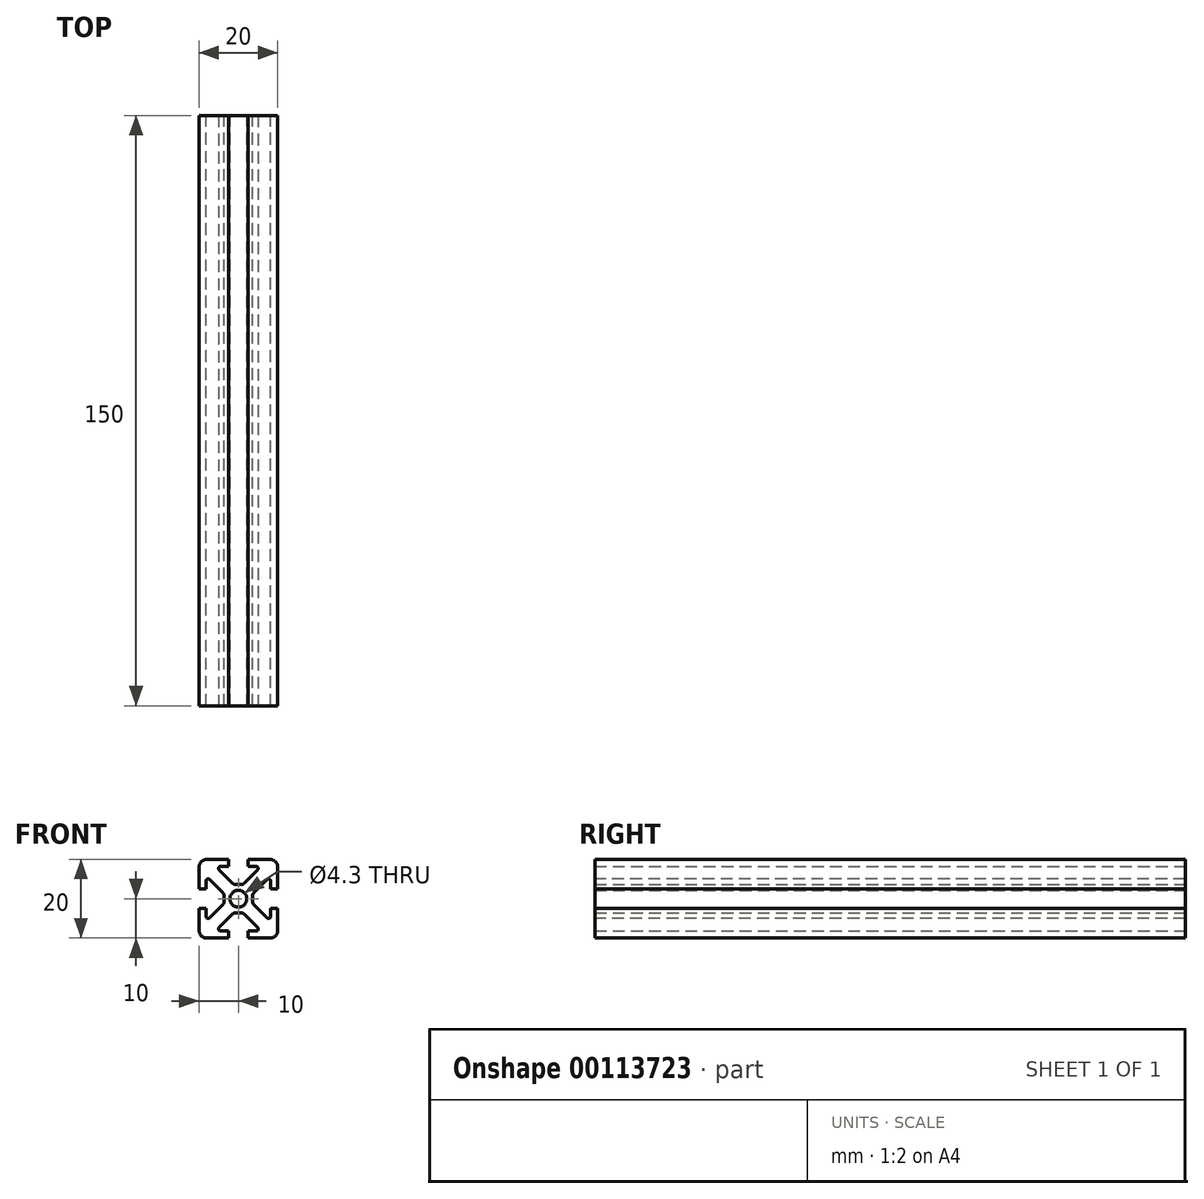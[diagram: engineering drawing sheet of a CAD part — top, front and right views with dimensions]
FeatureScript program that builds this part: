
annotation { "Feature Type Name" : "Feature", "Feature Type Description" : "" }
export const myFeature = defineFeature(function(context is Context, id is Id, definition is map)
    precondition{}
    {
        {
            var Q0;
            Q0=qCreatedBy(makeId("Front.planeOp"),FACE);
            var sketch = newSketch(context, id + "F0", { "sketchPlane" : qUnion([Q0])});
            skLineSegment(sketch, "E0.bottom", {"start": v(-10, 10) * mm, "end": v(10, 10) * mm});
            skLineSegment(sketch, "E0.top", {"start": v(-10, -10) * mm, "end": v(10, -10) * mm});
            skLineSegment(sketch, "E0.left", {"start": v(-10, 10) * mm, "end": v(-10, -10) * mm});
            skLineSegment(sketch, "E0.right", {"start": v(10, 10) * mm, "end": v(10, -10) * mm});
            skLineSegment(sketch, "E1", {"start": v(0, 10) * mm, "end": v(0, -10) * mm, "construction": true});
            skLineSegment(sketch, "E2", {"start": v(-10, 10) * mm, "end": v(10, -10) * mm, "construction": true});
            skLineSegment(sketch, "E3", {"start": v(-10, 0) * mm, "end": v(10, 0) * mm, "construction": true});
            skLineSegment(sketch, "E4", {"start": v(-2.5, 10) * mm, "end": v(-2.5, 8.2) * mm});
            skLineSegment(sketch, "E5", {"start": v(-2.5, 8.2) * mm, "end": v(-5.75, 8.2) * mm});
            skLineSegment(sketch, "E6", {"start": v(-5.75, 8.2) * mm, "end": v(-1.2, 3.65) * mm});
            skLineSegment(sketch, "E7", {"start": v(-1.2, 3.65) * mm, "end": v(0, 3.65) * mm});
            skLineSegment(sketch, "E8.MirrorCS", {"start": v(-10, 2.5) * mm, "end": v(-8.2, 2.5) * mm});
            skLineSegment(sketch, "E9.MirrorCS", {"start": v(-3.65, 1.2) * mm, "end": v(-3.65, 0) * mm});
            skLineSegment(sketch, "E10.MirrorCS", {"start": v(-8.2, 2.5) * mm, "end": v(-8.2, 5.75) * mm});
            skLineSegment(sketch, "E11.MirrorCS", {"start": v(-8.2, 5.75) * mm, "end": v(-3.65, 1.2) * mm});
            skLineSegment(sketch, "E12.MirrorCS", {"start": v(2.5, 10) * mm, "end": v(2.5, 8.2) * mm});
            skLineSegment(sketch, "E13.MirrorCS", {"start": v(5.75, 8.2) * mm, "end": v(1.2, 3.65) * mm});
            skLineSegment(sketch, "E14.MirrorCS", {"start": v(2.5, 8.2) * mm, "end": v(5.75, 8.2) * mm});
            skLineSegment(sketch, "E15.MirrorCS", {"start": v(1.2, 3.65) * mm, "end": v(0, 3.65) * mm});
            skLineSegment(sketch, "E16.MirrorCS", {"start": v(8.2, 2.5) * mm, "end": v(8.2, 5.75) * mm});
            skLineSegment(sketch, "E17.MirrorCS", {"start": v(8.2, 5.75) * mm, "end": v(3.65, 1.2) * mm});
            skLineSegment(sketch, "E18.MirrorCS", {"start": v(3.65, 1.2) * mm, "end": v(3.65, 0) * mm});
            skLineSegment(sketch, "E19.MirrorCS", {"start": v(10, 2.5) * mm, "end": v(8.2, 2.5) * mm});
            skLineSegment(sketch, "E20.MirrorCS", {"start": v(2.5, -8.2) * mm, "end": v(5.75, -8.2) * mm});
            skLineSegment(sketch, "E21.MirrorCS", {"start": v(2.5, -10) * mm, "end": v(2.5, -8.2) * mm});
            skLineSegment(sketch, "E22.MirrorCS", {"start": v(10, -2.5) * mm, "end": v(8.2, -2.5) * mm});
            skLineSegment(sketch, "E23.MirrorCS", {"start": v(8.2, -5.75) * mm, "end": v(3.65, -1.2) * mm});
            skLineSegment(sketch, "E24.MirrorCS", {"start": v(1.2, -3.65) * mm, "end": v(0, -3.65) * mm});
            skLineSegment(sketch, "E25.MirrorCS", {"start": v(5.75, -8.2) * mm, "end": v(1.2, -3.65) * mm});
            skLineSegment(sketch, "E26.MirrorCS", {"start": v(3.65, -1.2) * mm, "end": v(3.65, 0) * mm});
            skLineSegment(sketch, "E27.MirrorCS", {"start": v(8.2, -2.5) * mm, "end": v(8.2, -5.75) * mm});
            skLineSegment(sketch, "E28.MirrorCS", {"start": v(-2.5, -10) * mm, "end": v(-2.5, -8.2) * mm});
            skLineSegment(sketch, "E29.MirrorCS", {"start": v(-1.2, -3.65) * mm, "end": v(0, -3.65) * mm});
            skLineSegment(sketch, "E30.MirrorCS", {"start": v(-5.75, -8.2) * mm, "end": v(-1.2, -3.65) * mm});
            skLineSegment(sketch, "E31.MirrorCS", {"start": v(-2.5, -8.2) * mm, "end": v(-5.75, -8.2) * mm});
            skLineSegment(sketch, "E32.MirrorCS", {"start": v(-8.2, -5.75) * mm, "end": v(-3.65, -1.2) * mm});
            skLineSegment(sketch, "E33.MirrorCS", {"start": v(-8.2, -2.5) * mm, "end": v(-8.2, -5.75) * mm});
            skLineSegment(sketch, "E34.MirrorCS", {"start": v(-10, -2.5) * mm, "end": v(-8.2, -2.5) * mm});
            skLineSegment(sketch, "E35.MirrorCS", {"start": v(-3.65, -1.2) * mm, "end": v(-3.65, 0) * mm});
            skCircle(sketch, "E36", {"center": v(0, 0) * mm, "radius": 2.15 * mm});
            skSolve(sketch);
        }
        {
            var Q0;
            Q0=makeQuery(id+"F0.imprint","IMPRINT",FACE,{"disambiguationData":[TD([[makeQuery(id+"F0.imprint","IMPRINT",EDGE,{"derivedFrom":sQuery(id+"F0.wireOp",EDGE,"E0.bottom")}),-1.0]])]});
            extrude(context, id + "F1", {"entities" : qUnion([Q0]), "depth" : 150 * mm});
        }
        {
            var Q0;
            Q0=makeQuery(id+"F1.opExtrude","SWEPT_EDGE",EDGE,{"disambiguationData":[OSD([sQuery(id+"F0.wireOp",EDGE,"E0.bottom"),sQuery(id+"F0.wireOp",EDGE,"E0.left")])]});
            var Q1;
            Q1=makeQuery(id+"F1.opExtrude","SWEPT_EDGE",EDGE,{"disambiguationData":[OSD([sQuery(id+"F0.wireOp",EDGE,"E0.bottom"),sQuery(id+"F0.wireOp",EDGE,"E0.right")])]});
            var Q2;
            Q2=makeQuery(id+"F1.opExtrude","SWEPT_EDGE",EDGE,{"disambiguationData":[OSD([sQuery(id+"F0.wireOp",EDGE,"E0.top"),sQuery(id+"F0.wireOp",EDGE,"E0.right")])]});
            var Q3;
            Q3=makeQuery(id+"F1.opExtrude","SWEPT_EDGE",EDGE,{"disambiguationData":[OSD([sQuery(id+"F0.wireOp",EDGE,"E0.top"),sQuery(id+"F0.wireOp",EDGE,"E0.left")])]});
            fillet(context, id + "F2", {"entities" : qUnion([Q0, Q1, Q2, Q3]), "radius" : 2 * mm, "tangentPropagation" : true, "allowEdgeOverflow" : false});
        }
        {
            var Q0;
            Q0=makeQuery(id+"F1.opExtrude","SWEPT_EDGE",EDGE,{"disambiguationData":[OSD([sQuery(id+"F0.wireOp",EDGE,"E32.MirrorCS"),sQuery(id+"F0.wireOp",EDGE,"E33.MirrorCS")])]});
            var Q1;
            Q1=makeQuery(id+"F1.opExtrude","SWEPT_EDGE",EDGE,{"disambiguationData":[OSD([sQuery(id+"F0.wireOp",EDGE,"E23.MirrorCS"),sQuery(id+"F0.wireOp",EDGE,"E27.MirrorCS")])]});
            var Q2;
            Q2=makeQuery(id+"F1.opExtrude","SWEPT_EDGE",EDGE,{"disambiguationData":[OSD([sQuery(id+"F0.wireOp",EDGE,"E13.MirrorCS"),sQuery(id+"F0.wireOp",EDGE,"E14.MirrorCS")])]});
            var Q3;
            Q3=makeQuery(id+"F1.opExtrude","SWEPT_EDGE",EDGE,{"disambiguationData":[OSD([sQuery(id+"F0.wireOp",EDGE,"E20.MirrorCS"),sQuery(id+"F0.wireOp",EDGE,"E25.MirrorCS")])]});
            var Q4;
            Q4=makeQuery(id+"F1.opExtrude","SWEPT_EDGE",EDGE,{"disambiguationData":[OSD([sQuery(id+"F0.wireOp",EDGE,"E5"),sQuery(id+"F0.wireOp",EDGE,"E6")])]});
            var Q5;
            Q5=makeQuery(id+"F1.opExtrude","SWEPT_EDGE",EDGE,{"disambiguationData":[OSD([sQuery(id+"F0.wireOp",EDGE,"E30.MirrorCS"),sQuery(id+"F0.wireOp",EDGE,"E31.MirrorCS")])]});
            var Q6;
            Q6=makeQuery(id+"F1.opExtrude","SWEPT_EDGE",EDGE,{"disambiguationData":[OSD([sQuery(id+"F0.wireOp",EDGE,"E16.MirrorCS"),sQuery(id+"F0.wireOp",EDGE,"E17.MirrorCS")])]});
            var Q7;
            Q7=makeQuery(id+"F1.opExtrude","SWEPT_EDGE",EDGE,{"disambiguationData":[OSD([sQuery(id+"F0.wireOp",EDGE,"E10.MirrorCS"),sQuery(id+"F0.wireOp",EDGE,"E11.MirrorCS")])]});
            fillet(context, id + "F3", {"entities" : qUnion([Q0, Q1, Q2, Q3, Q4, Q5, Q6, Q7]), "radius" : 0.5 * mm, "tangentPropagation" : true, "allowEdgeOverflow" : false});
        }
        {
            var Q0;
            Q0=makeQuery(id+"F1.opExtrude","SWEPT_EDGE",EDGE,{"disambiguationData":[OSD([sQuery(id+"F0.wireOp",EDGE,"E6"),sQuery(id+"F0.wireOp",EDGE,"E7")])]});
            var Q1;
            Q1=makeQuery(id+"F1.opExtrude","SWEPT_EDGE",EDGE,{"disambiguationData":[OSD([sQuery(id+"F0.wireOp",EDGE,"E23.MirrorCS"),sQuery(id+"F0.wireOp",EDGE,"E26.MirrorCS")])]});
            var Q2;
            Q2=makeQuery(id+"F1.opExtrude","SWEPT_EDGE",EDGE,{"disambiguationData":[OSD([sQuery(id+"F0.wireOp",EDGE,"E13.MirrorCS"),sQuery(id+"F0.wireOp",EDGE,"E15.MirrorCS")])]});
            var Q3;
            Q3=makeQuery(id+"F1.opExtrude","SWEPT_EDGE",EDGE,{"disambiguationData":[OSD([sQuery(id+"F0.wireOp",EDGE,"E9.MirrorCS"),sQuery(id+"F0.wireOp",EDGE,"E11.MirrorCS")])]});
            var Q4;
            Q4=makeQuery(id+"F1.opExtrude","SWEPT_EDGE",EDGE,{"disambiguationData":[OSD([sQuery(id+"F0.wireOp",EDGE,"E32.MirrorCS"),sQuery(id+"F0.wireOp",EDGE,"E35.MirrorCS")])]});
            var Q5;
            Q5=makeQuery(id+"F1.opExtrude","SWEPT_EDGE",EDGE,{"disambiguationData":[OSD([sQuery(id+"F0.wireOp",EDGE,"E24.MirrorCS"),sQuery(id+"F0.wireOp",EDGE,"E25.MirrorCS")])]});
            var Q6;
            Q6=makeQuery(id+"F1.opExtrude","SWEPT_EDGE",EDGE,{"disambiguationData":[OSD([sQuery(id+"F0.wireOp",EDGE,"E29.MirrorCS"),sQuery(id+"F0.wireOp",EDGE,"E30.MirrorCS")])]});
            var Q7;
            Q7=makeQuery(id+"F1.opExtrude","SWEPT_EDGE",EDGE,{"disambiguationData":[OSD([sQuery(id+"F0.wireOp",EDGE,"E17.MirrorCS"),sQuery(id+"F0.wireOp",EDGE,"E18.MirrorCS")])]});
            fillet(context, id + "F4", {"entities" : qUnion([Q0, Q1, Q2, Q3, Q4, Q5, Q6, Q7]), "radius" : 0.8 * mm, "tangentPropagation" : true, "allowEdgeOverflow" : false});
        }
    });
